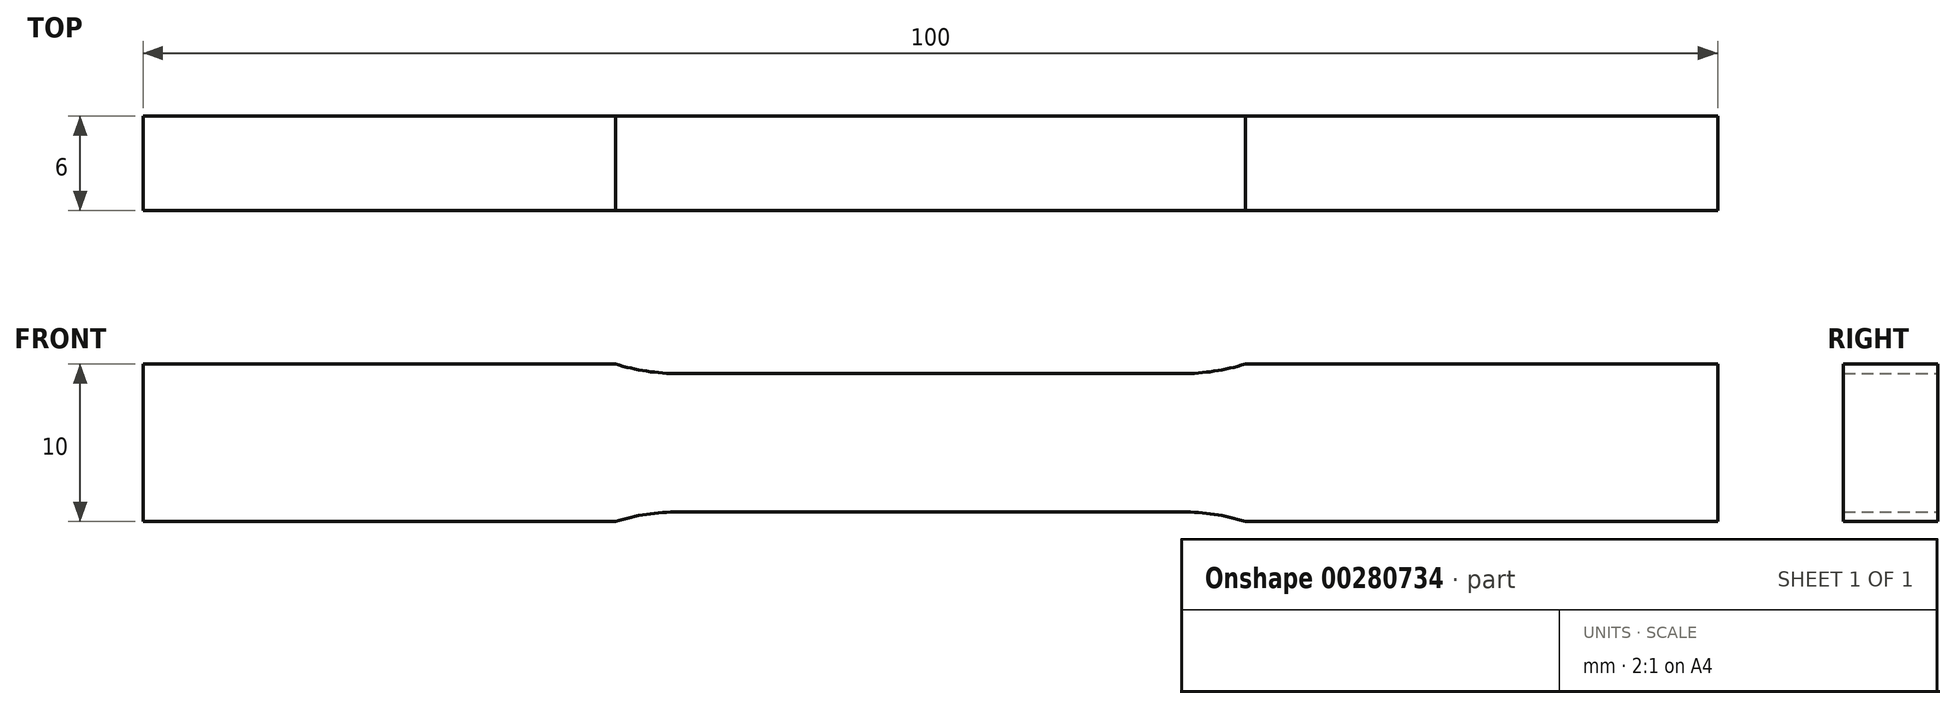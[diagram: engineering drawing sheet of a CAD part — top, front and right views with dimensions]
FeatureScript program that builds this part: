
annotation { "Feature Type Name" : "Feature", "Feature Type Description" : "" }
export const myFeature = defineFeature(function(context is Context, id is Id, definition is map)
    precondition{}
    {
        {
            var Q0;
            Q0=qCreatedBy(makeId("Front.planeOp"),FACE);
            var sketch = newSketch(context, id + "F0", { "sketchPlane" : qUnion([Q0])});
            skLineSegment(sketch, "E0", {"start": v(0, 4.4) * mm, "end": v(16, 4.4) * mm});
            skArc(sketch, "E1", {"start": v(16, 4.4) * mm, "mid": v(18.02, 4.55) * mm, "end": v(20, 5) * mm});
            skLineSegment(sketch, "E2", {"start": v(20, 5) * mm, "end": v(50, 5) * mm});
            skLineSegment(sketch, "E3", {"start": v(50, 5) * mm, "end": v(50, 0) * mm});
            skLineSegment(sketch, "E4.MirrorCS", {"start": v(0, 4.4) * mm, "end": v(-16, 4.4) * mm});
            skLineSegment(sketch, "E5.MirrorCS", {"start": v(-20, 5) * mm, "end": v(-50, 5) * mm});
            skLineSegment(sketch, "E6.MirrorCS", {"start": v(-50, 5) * mm, "end": v(-50, 0) * mm});
            skArc(sketch, "E7.MirrorCS", {"start": v(-16, 4.4) * mm, "mid": v(-18.02, 4.55) * mm, "end": v(-20, 5) * mm});
            skArc(sketch, "E8.MirrorCS", {"start": v(-16, -4.4) * mm, "mid": v(-18.02, -4.55) * mm, "end": v(-20, -5) * mm});
            skLineSegment(sketch, "E9.MirrorCS", {"start": v(-50, -5) * mm, "end": v(-50, 0) * mm});
            skArc(sketch, "E10.MirrorCS", {"start": v(16, -4.4) * mm, "mid": v(18.02, -4.55) * mm, "end": v(20, -5) * mm});
            skLineSegment(sketch, "E11.MirrorCS", {"start": v(20, -5) * mm, "end": v(50, -5) * mm});
            skLineSegment(sketch, "E12.MirrorCS", {"start": v(-20, -5) * mm, "end": v(-50, -5) * mm});
            skLineSegment(sketch, "E13.MirrorCS", {"start": v(0, -4.4) * mm, "end": v(16, -4.4) * mm});
            skLineSegment(sketch, "E14.MirrorCS", {"start": v(0, -4.4) * mm, "end": v(-16, -4.4) * mm});
            skLineSegment(sketch, "E15.MirrorCS", {"start": v(50, -5) * mm, "end": v(50, 0) * mm});
            skSolve(sketch);
        }
        {
            var Q0;
            Q0 = qSketchRegion(id + "F0", true);
            extrude(context, id + "F1", {"entities" : qUnion([Q0]), "endBound" : BoundingType.SYMMETRIC, "depth" : 6 * mm});
        }
    });
